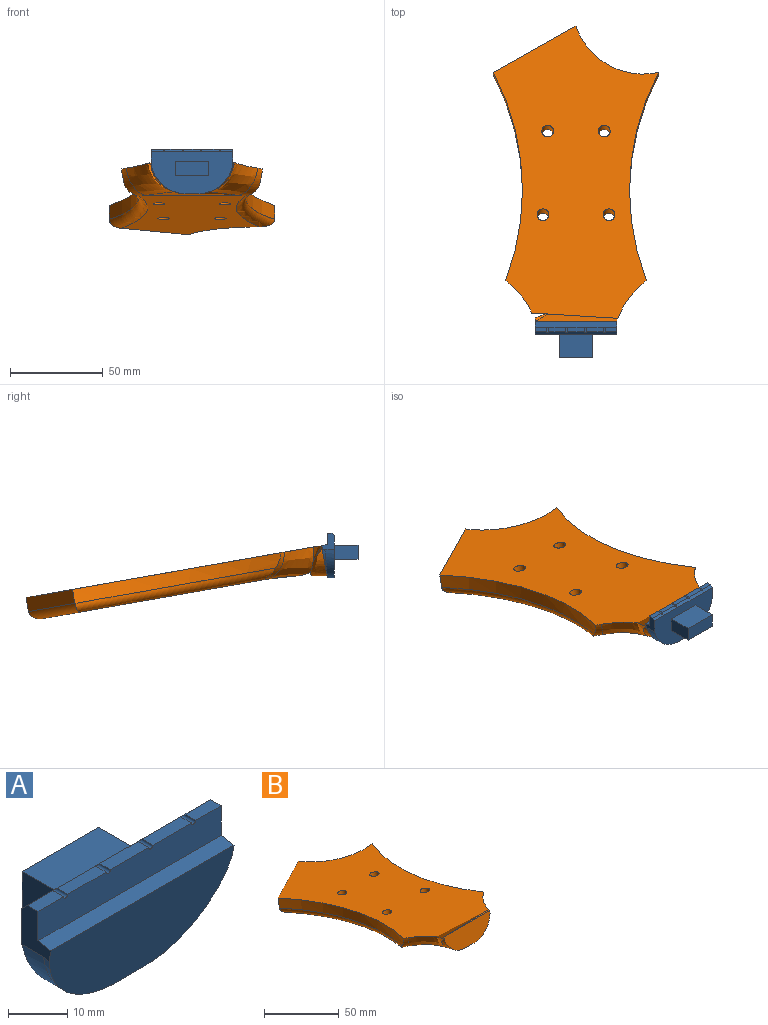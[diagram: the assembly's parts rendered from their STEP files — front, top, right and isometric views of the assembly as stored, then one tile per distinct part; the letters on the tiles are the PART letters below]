
ASSEMBLY  parts=2 mates=1
PART A: 34 faces, bbox 43.7x19.6x24 mm
  f0: plane 9.14x2.54mm, normal (0,0,1), area 23.2mm2, adj f4,f26,f27,f33
  f1: plane 9.14x2.54mm, normal (0,0,1), area 23.2mm2, adj f4,f24,f25,f33
  f2: plane 9.14x2.54mm, normal (0,0,1), area 23.2mm2, adj f4,f22,f23,f33
  f3: plane 6.09x2.54mm, normal (0,0,1), area 15.5mm2, adj f4,f7,f21,f33
  f4: plane 43.68x6.08mm, normal (0,-1,0), area 263.9mm2, adj f0,f1,f2,f3,f7,f8,f18,f20
  f5: plane 6.35x3.81mm, normal (0,0,-1), area 24.2mm2, adj f6,f9,f10,f19
  f6: cylinder r=19.05mm len=18.67mm, axis (0,1,0), area 111.8mm2, adj f5,f7,f10,f16
  f7: plane 8.96x6.87mm, normal (1,0,0), area 39.5mm2, adj f3,f4,f6,f10,f16,f18,f19,f33
  f8: plane 8.96x6.87mm, normal (-1,0,0), area 39.5mm2, adj f4,f9,f10,f17,f18,f19,f20,f33
  f9: cylinder r=19.05mm len=18.67mm, axis (0,1,0), area 111.8mm2, adj f5,f8,f10,f17
  f10: plane 43.68x22.7mm, normal (0,1,0), area 709.2mm2, adj f5,f6,f7,f8,f9,f11,f12,f13
  f11: plane 18.28x12.7mm, normal (0,0,1), area 232.2mm2, adj f10,f12,f14,f15
  f12: plane 12.7x7.62mm, normal (1,0,0), area 96.8mm2, adj f10,f11,f13,f15
  f13: plane 18.28x12.7mm, normal (0,0,-1), area 232.2mm2, adj f10,f12,f14,f15
  f14: plane 12.7x7.62mm, normal (-1,0,0), area 96.8mm2, adj f10,f11,f13,f15
  f15: plane 18.28x7.62mm, normal (0,1,0), area 139.3mm2, adj f11,f12,f13,f14
  f16: cylinder r=19.05mm len=18.67mm, axis (0,-0.98,-0.17), area 12.4mm2, adj f6,f7,f19
  f17: cylinder r=19.05mm len=18.67mm, axis (0,-0.98,-0.17), area 12.4mm2, adj f8,f9,f19
  f18: plane 43.68x3.06mm, normal (0,-0.17,0.98), area 135.7mm2, adj f4,f7,f8,f19
  f19: plane 43.68x17.35mm, normal (0,-0.98,-0.17), area 626.6mm2, adj f5,f7,f8,f16,f17,f18
  f20: plane 6.09x2.54mm, normal (0,0,1), area 15.5mm2, adj f4,f8,f28,f33
  f21: plane 2.54x0mm, normal (-1,0,0), area 0mm2, adj f3,f4,f31,f33
  f22: plane 2.54x0mm, normal (1,0,0), area 0mm2, adj f2,f4,f31,f33
  f23: plane 2.54x0mm, normal (-1,0,0), area 0mm2, adj f2,f4,f30,f33
  f24: plane 2.54x0mm, normal (1,0,0), area 0mm2, adj f1,f4,f30,f33
  f25: plane 2.54x0mm, normal (-1,0,0), area 0mm2, adj f1,f4,f29,f33
  f26: plane 2.54x0mm, normal (1,0,0), area 0mm2, adj f0,f4,f29,f33
  f27: plane 2.54x0mm, normal (-1,0,0), area 0mm2, adj f0,f4,f32,f33
  f28: plane 2.54x0mm, normal (1,0,0), area 0mm2, adj f4,f20,f32,f33
  f29: cylinder r=0.51mm len=3.05mm, axis (0,-1,0), area 4.6mm2, adj f4,f25,f26,f33
  f30: cylinder r=0.51mm len=3.05mm, axis (0,-1,0), area 4.6mm2, adj f4,f23,f24,f33
  f31: cylinder r=0.51mm len=3.05mm, axis (0,-1,0), area 4.6mm2, adj f4,f21,f22,f33
  f32: cylinder r=0.51mm len=3.05mm, axis (0,-1,0), area 4.6mm2, adj f4,f27,f28,f33
  f33: plane 43.68x1.27mm, normal (0,0.71,0.71), area 76.1mm2, adj f0,f1,f2,f3,f7,f8,f10,f20
PART B: 23 faces, bbox 111.3x185.9x62.3 mm
  f0: bspline ~18.56x16.34mm, area 156.6mm2, adj f1,f2,f18
  f1: plane 160.36x90.12mm, normal (0,0.17,0.98), area 9425mm2, adj f0,f3,f5,f6,f7,f8,f14,f15
  f2: plane 50.17x31.21mm, normal (0,0,-1), area 115mm2, adj f0,f3,f9,f18
  f3: bspline ~18.56x16.34mm, area 156.6mm2, adj f1,f2,f18
  f4: plane 119.88x73.74mm, normal (0,-0.17,-0.98), area 5861.3mm2, adj f9,f10,f11,f12,f13,f15,f17,f19
  f5: cylinder r=38.1mm len=44.45mm, axis (0,0.17,0.98), area 427.8mm2, adj f1,f7,f8,f12
  f6: cylinder r=139.7mm len=113.46mm, axis (0,0.17,0.98), area 878.8mm2, adj f1,f8,f10,f15
  f7: cylinder r=139.7mm len=113.46mm, axis (0,0.17,0.98), area 878.8mm2, adj f1,f5,f13,f17
  f8: plane 44.45x26.34mm, normal (-0.5,0.86,-0.15), area 390.1mm2, adj f1,f5,f6,f11
  f9: cylinder r=127mm len=50.1mm, axis (-1,0,0), area 710.6mm2, adj f2,f4,f14,f16
  f10: torus R=144.78mm, axis (0,-0.17,-0.98), area 852.4mm2, adj f4,f6,f11,f15
  f11: cylinder r=5.08mm len=46.97mm, axis (0.87,0.49,-0.09), area 366.3mm2, adj f4,f8,f10,f12
  f12: torus R=43.18mm, axis (0,-0.17,-0.98), area 410mm2, adj f4,f5,f11,f13
  f13: torus R=144.78mm, axis (0,-0.17,-0.98), area 835.4mm2, adj f4,f7,f12,f17
  f14: bspline ~36.74x34.88mm, area 586.9mm2, adj f1,f9,f15
  f15: torus R=64.13mm, axis (0,-0.17,-0.98), area 99.4mm2, adj f1,f4,f6,f10,f14
  f16: bspline ~36.74x34.88mm, area 586.9mm2, adj f1,f9,f17
  f17: torus R=64.13mm, axis (0,-0.17,-0.98), area 99.4mm2, adj f1,f4,f7,f13,f16
  f18: plane 43.69x16.24mm, normal (0,-0.98,0.17), area 581.4mm2, adj f0,f1,f2,f3
  f19: cylinder r=3.17mm len=13.61mm, axis (0,0.17,0.98), area 253.4mm2, adj f1,f4
  f20: cylinder r=3.17mm len=13.61mm, axis (0,0.17,0.98), area 253.4mm2, adj f1,f4
  f21: cylinder r=3.17mm len=13.61mm, axis (0,0.17,0.98), area 253.4mm2, adj f1,f4
  f22: cylinder r=3.17mm len=13.61mm, axis (0,0.17,0.98), area 253.4mm2, adj f1,f4
PLACE A rot(axis=(0,0,-1),180deg) t=(94.72,58.26,18.95)mm
PLACE B t=(46.69,-411.4,2.44)mm
MATE fastened B.f18 <-> A.f19  axis (0,-0.98,0.17) through (72.88,65.13,18.68)mm
